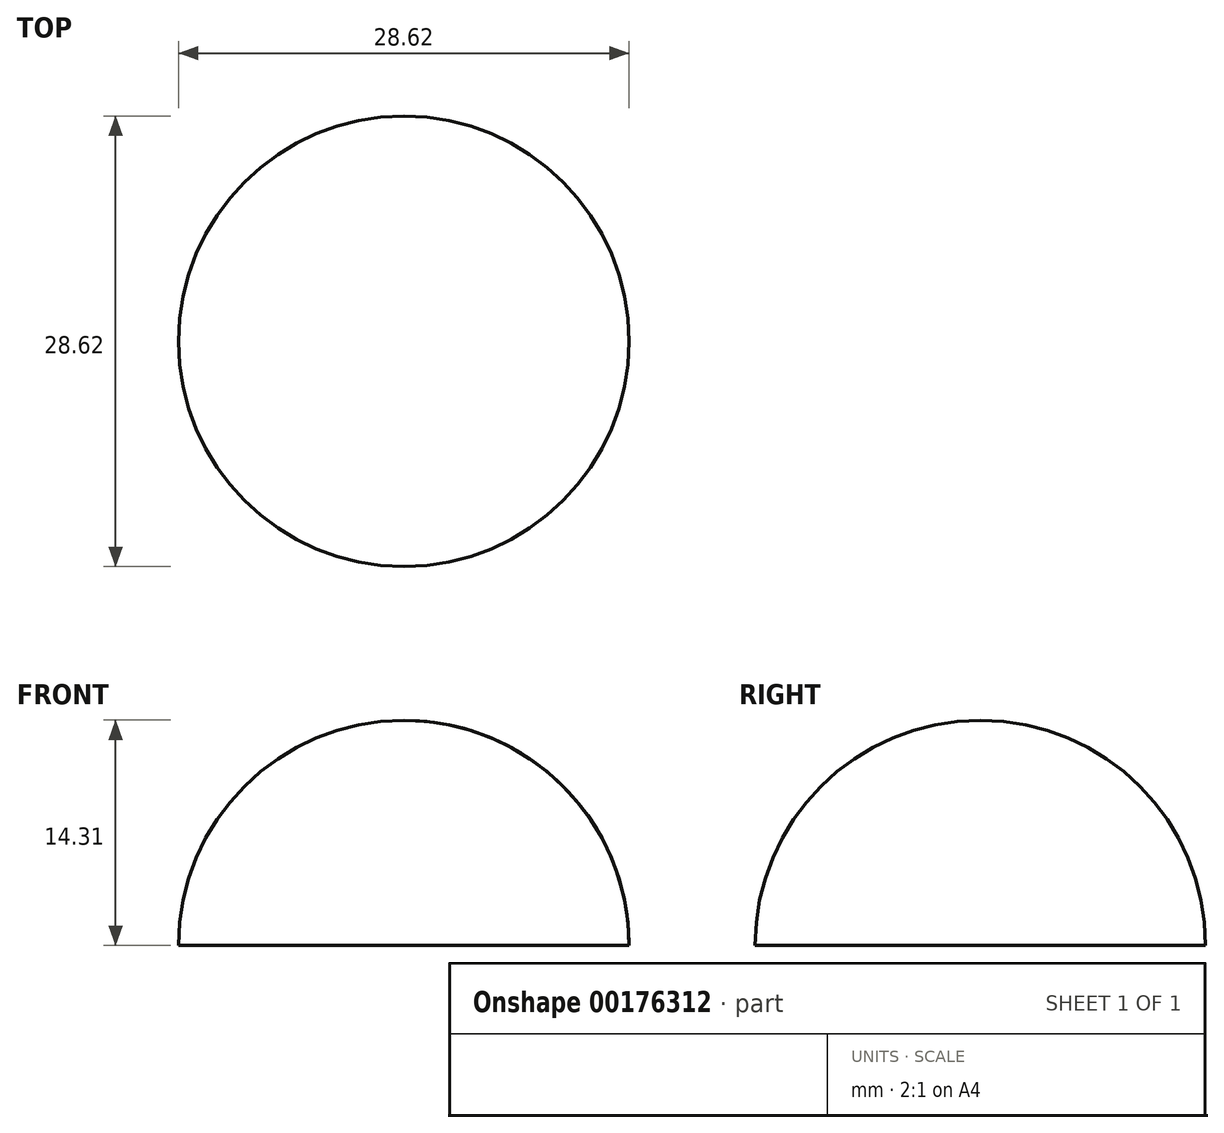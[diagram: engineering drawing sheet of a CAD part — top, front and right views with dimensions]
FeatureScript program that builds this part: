
annotation { "Feature Type Name" : "Feature", "Feature Type Description" : "" }
export const myFeature = defineFeature(function(context is Context, id is Id, definition is map)
    precondition{}
    {
        {
            var Q0;
            Q0=qCreatedBy(makeId("Front.planeOp"),FACE);
            var sketch = newSketch(context, id + "F0", { "sketchPlane" : qUnion([Q0])});
            skArc(sketch, "E0", {"start": v(14.3, 0) * mm, "mid": v(10.12, 10.12) * mm, "end": v(0, 14.3) * mm});
            skLineSegment(sketch, "E1", {"start": v(0, 14.3) * mm, "end": v(0, 0) * mm});
            skLineSegment(sketch, "E2", {"start": v(0, 0) * mm, "end": v(14.3, 0) * mm});
            skSolve(sketch);
        }
        {
            var Q0;
            Q0 = qSketchRegion(id + "F0", true);
            var Q1;
            Q1=sQuery(id+"F0.wireOp",EDGE,"E1");
            revolve(context, id + "F1", {"entities" : qUnion([Q0]), "axis" : qUnion([Q1]), "revolveType" : RevolveType.FULL});
        }
    });
